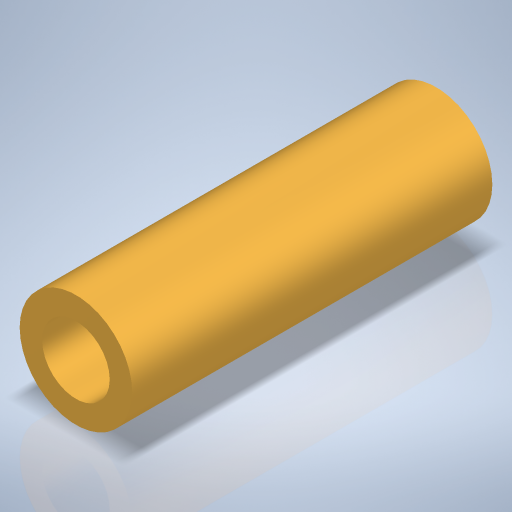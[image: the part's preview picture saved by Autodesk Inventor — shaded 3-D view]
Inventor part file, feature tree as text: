
AUTODESK INVENTOR PART (.ipt)
format: ipt  version: 2024 (Build 280153000, 153)  size: 237,056 bytes
history: native  units: mm
features: extrude x1, sketch x1
ambient origin geometry x8: Origin, YZ Plane, XZ Plane, XY Plane, X Axis, Y Axis, Z Axis, Center Point
bodies: Volumenkörper1 (feature_tree)
feature tree (2):
  extrude  "Extrusion1"  Depth=16.0mm
  sketch  "Skizze1"  dims[d0=5.0mm d1=3.0mm d2=16.0mm d3=0.0mm]
